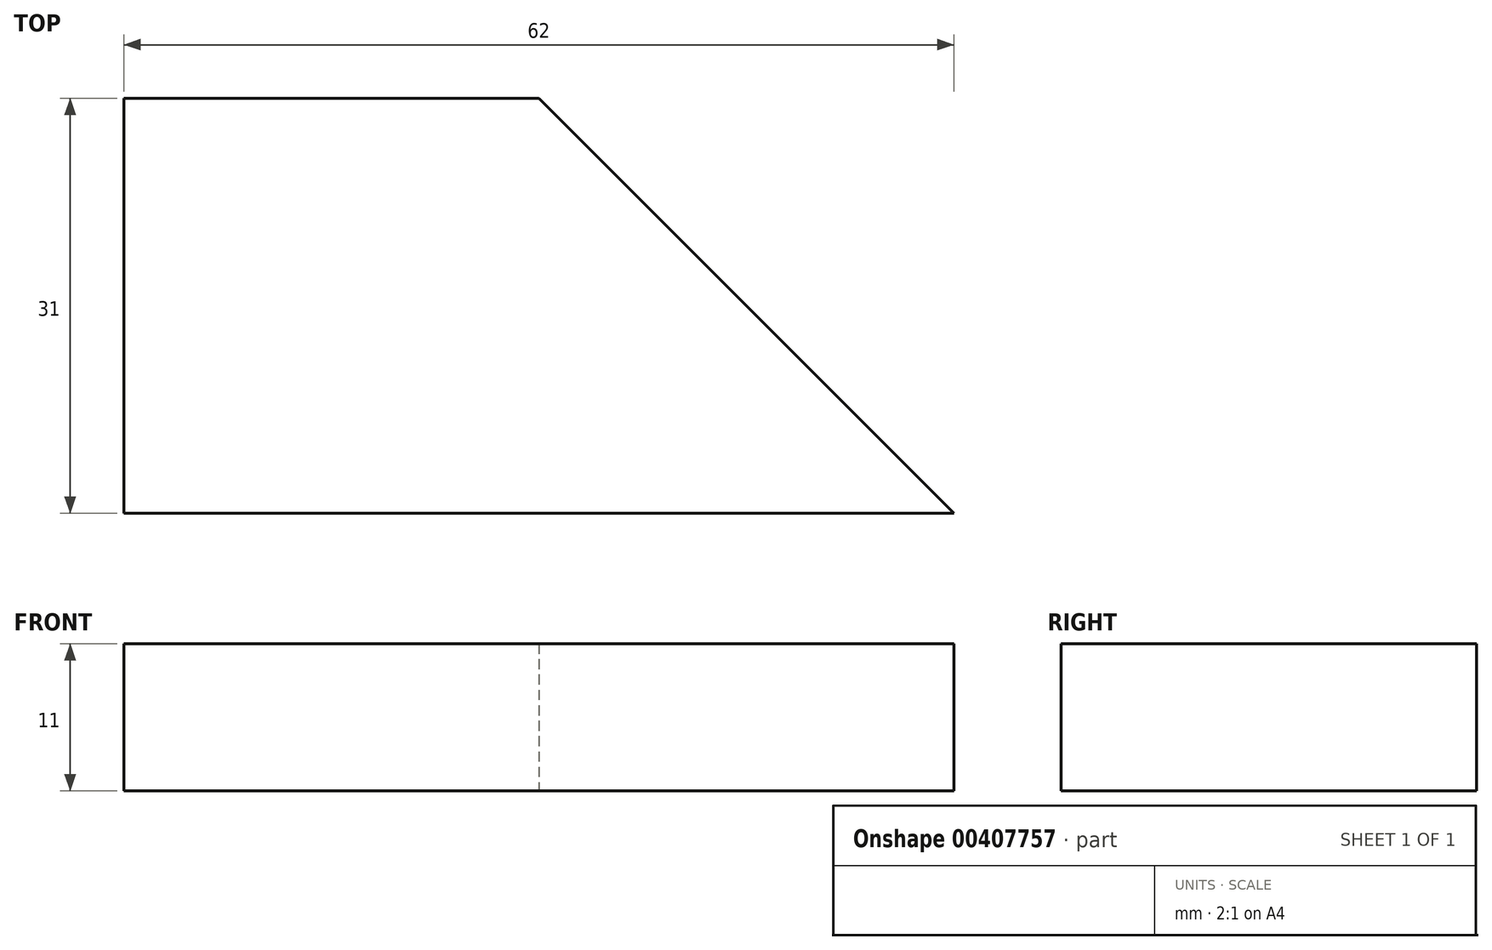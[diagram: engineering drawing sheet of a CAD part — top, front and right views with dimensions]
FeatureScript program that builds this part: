
annotation { "Feature Type Name" : "Feature", "Feature Type Description" : "" }
export const myFeature = defineFeature(function(context is Context, id is Id, definition is map)
    precondition{}
    {
        {
            var Q0;
            Q0=qCreatedBy(makeId("Top.planeOp"),FACE);
            var sketch = newSketch(context, id + "F0", { "sketchPlane" : qUnion([Q0])});
            skLineSegment(sketch, "E0.bottom", {"start": v(-48.58, 31.3) * mm, "end": v(-17.58, 31.3) * mm});
            skLineSegment(sketch, "E0.top", {"start": v(-48.58, 62.3) * mm, "end": v(-17.58, 62.3) * mm});
            skLineSegment(sketch, "E0.left", {"start": v(-48.58, 31.3) * mm, "end": v(-48.58, 62.3) * mm});
            skLineSegment(sketch, "E1", {"start": v(-17.58, 62.3) * mm, "end": v(13.42, 31.3) * mm});
            skLineSegment(sketch, "E2", {"start": v(13.42, 31.3) * mm, "end": v(-17.58, 31.3) * mm});
            skSolve(sketch);
        }
        {
            var Q0;
            Q0=makeQuery(id+"F0.imprint","IMPRINT",FACE,{"disambiguationData":[TD([[makeQuery(id+"F0.imprint","IMPRINT",EDGE,{"derivedFrom":sQuery(id+"F0.wireOp",EDGE,"E0.bottom")}),1.0]])]});
            extrude(context, id + "F1", {"entities" : qUnion([Q0]), "depth" : 11 * mm});
        }
    });
